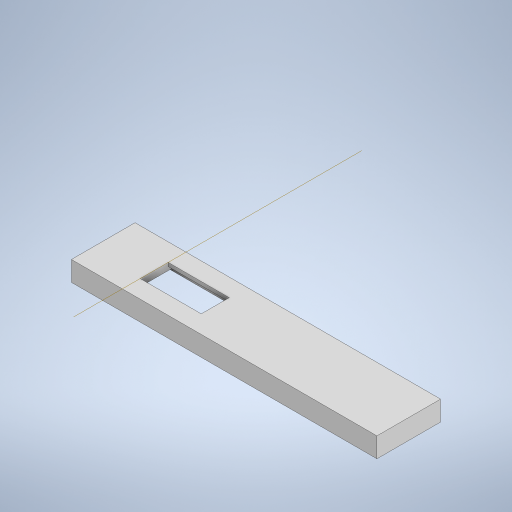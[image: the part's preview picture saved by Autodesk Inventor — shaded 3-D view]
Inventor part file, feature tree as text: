
AUTODESK INVENTOR PART (.ipt)
format: ipt  version: 2023 (Build 270158000, 158)  size: 436,224 bytes
history: native  units: in
note: dims shown in document units (in); Inventor stores cm internally (conversion verified against a paired STEP export)
features: extrude x9, sketch x9, plane x1
ambient origin geometry x8: Origin, YZ Plane, XZ Plane, XY Plane, X Axis, Y Axis, Z Axis, Center Point
bodies: Solid1 (feature_tree)
feature tree (19):
  extrude  "Extrusion1"  Depth=1.25in
  extrude  "Extrusion2"  Depth=0.55in
  extrude  "Extrusion3"  Depth=0.07in TaperAngle=0.0deg
  extrude  "Extrusion4"  TaperAngle=0.0deg  [1 undecoded]
  extrude  "Extrusion5"  Depth=0.0625in
  extrude  "Extrusion6"  Depth=0.25in
  plane  "Work Plane1"
  extrude  "Extrusion7"  Depth=0.1in
  extrude  "Extrusion8"  Depth=0.1in
  extrude  "Extrusion9"  Depth=0.06in
  sketch  "Sketch1"  dims[d0=6.0in d1=1.25in]
  sketch  "Sketch2"  dims[d2=1.2in d3=0.55in]
  sketch  "Sketch3"  dims[d4=1.0in d5=0.07in d6=0.0in]
  sketch  "Sketch4"  dims[d7=1.2in d8=0.0in]
  sketch  "Sketch5"  dims[d9=0.07in d10=0.0in d11=0.0625in]
  sketch  "Sketch6"  dims[d12=0.25in d13=0.0in d14=0.25in]
  sketch  "Sketch7"  dims[d15=0.1in d16=0.1in]
  sketch  "Sketch8"  dims[d17=0.1in d18=0.1in]
  sketch  "Sketch9"  dims[d19=0.1in d20=0.1in d21=1.0in d22=0.1in d23=0.1in d24=0.1in d25=0.1in d26=0.1in d27=0.1in d28=0.1in d29=0.1in d30=0.1in d31=0.1in d32=0.1in d33=0.1in d34=1.0in d35=1.0in d36=1.0in d37=1.25in d38=0.0in d39=0.1in d40=0.1in d41=0.1in d42=0.1in d43=0.1in d44=0.1in d45=1.0in d46=1.0in d47=0.1in d48=0.1in d49=1.0in d50=0.1in d51=0.1in d52=1.0in d53=1.25in d54=0.0in d55=0.125in d56=0.0in d57=45.0deg d58=0.0in d59=5.0in d60=0.125in d61=0.0in d62=1.0in d63=0.0in d64=0.06in d65=0.0in]
note: 1 required parameter value undecoded (feature->parameter linkage not recoverable at this tier; creation-order binding heuristic only, values carry confidence <= 0.55)
